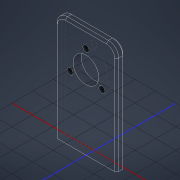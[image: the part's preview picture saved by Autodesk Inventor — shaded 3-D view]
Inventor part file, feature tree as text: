
AUTODESK INVENTOR PART (.ipt)
format: ipt  version: 2021 (Build 250183000, 183)  size: 183,296 bytes
history: native  units: mm
features: sketch x3, extrude x2, fillet x1, hole x1, chamfer x1
ambient origin geometry x8: Origin, YZ Plane, XZ Plane, XY Plane, X Axis, Y Axis, Z Axis, Center Point
bodies: Solid1 (feature_tree)
feature tree (8):
  extrude  "Extrusion1"  Depth=106.0mm
  fillet  "Fillet1"  Radius=30.0mm
  hole  "Hole1"  [1 undecoded]
  extrude  "Extrusion2"  TaperAngle=120.0deg  [1 undecoded]
  chamfer  "Chamfer1"  Angle=120.0deg  [1 undecoded]
  sketch  "Sketch1"  dims[d0=60.0mm d1=106.0mm d2=30.0mm]
  sketch  "Sketch2"  dims[d3=8.0mm d4=0.0mm d5=10.0mm]
  sketch  "Sketch3"  dims[d6=36.0mm d7=120.0deg d8=120.0deg d9=0.0mm d10=72.0mm d11=6.0mm d12=6.0mm d13=4.0mm d14=2.0mm d15=90.0deg d16=8.0mm d17=20.594885mm d18=72.0mm d19=0.0mm d20=25.0mm d21=0.0mm d22=0.0mm d23=2.0mm d24=2.0mm d25=45.0deg]
note: 3 required parameter values undecoded (feature->parameter linkage not recoverable at this tier; creation-order binding heuristic only, values carry confidence <= 0.55)
